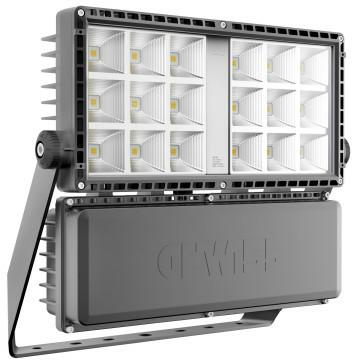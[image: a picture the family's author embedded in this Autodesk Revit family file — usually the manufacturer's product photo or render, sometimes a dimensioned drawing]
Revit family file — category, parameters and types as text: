
# Revit family: Lighting-Floodlights-GEWISS-SMART[PRO]2.0-LED-MEDIUM-POWER_2MODULE_DALI.CLI
name_source: partatom
category: Apparecchi per illuminazione
units: mm (PartAtom-declared; Revit-internal decimal feet)

## family parameters
Condiviso = No
Host = Superficie
Punto di calcolo locali = No
Quota connettore circolare = Usa diametro
Sorgente d'illuminazione = No
Taglio con vuoti quando caricato = No
Tipo di parte = Normale

## types (1)
- Lighting-Floodlights-GEWISS-SMART[PRO]2.0-LED-MEDIUM-POWER_2MODULE_DALI.CLI
    Applicazione = Indoor / Outdoor
    Body = Die-cast aluminium -
    Catalogue = LIGHTING
    Classification: = -
    Color Rendering Index = CRI-80
    Colour = Graphite grey
    Colour : = Polyester powder coated
    Colour temperature = 5700K
    Context = Sport, Big Areas
    Control System = DALI
    DIN 18032-3 certification = Yes
    Descrizione = SMARTPRO2.0 2M 5700K CRI80 A3 DALI CL1
    Device with reduced surface temperature = No
    Driver = Included
    Driver Box = Built-in
    Efficiency (lm/W) = 113
    Eletrical and lighting features = -
    External screw = Stainless steel
    Fixing = Bracket
    GW - Codice Electrocod = 2424
    Gasket = Anti-aging silicone
    General information = -
    Glow Wire Test : = -
    IDF = fea9197c-9a36-4712-b795-7101e1c42ea6
    IDT = 256691c01990452284852cf61e57a00c
    IP degree = IP66
    IPEA = ROAD = A // LARGE AREAS = A3 + // CYCLOPEDONALS = A + // GREEN AREAS = A + // HISTORICAL CENTER = A5 + // OTHER = A5 +
    Immagine tipo = GWP2274AD.jpg
    Installationa and maintenance = -
    Insulation class = I
    LED Maintenance = Not available
    Lampada = LED
    Lifetime = L90B10 (Tq+25°C) - 40000h L90B10 (Tq+50°C) = 32000h L80B10 (Tq+25°C) - 90000h
    Locking Hook = Hexagonal metric screws
    Lumen output (lm) = 37200
    Luminaire = LED luminaire with small,mid and high lumen power
    Materials = -
    Maximum surface exposed to the wind : = 0,170 m2
    Modello = GWP2285ND
    Mouting and installation = High-mast lighting - Wall mounting - Ground mouting
    Operating temperature : = -30 +50 °C
    Optic = A3 - Assymetric Narrow
    Optic : = Polished anodised aluminum reflector with 99.99% pure aluminum
    Optic Maintenance = Not available
    Optic and illuminating features = -
    Overvoltage protection = DM 6 kV / CM 10 kV
    Photobiological Risk Class = -
    Produttore = GEWISS S.p.A.
    Prospetto di default = 1219 mm
    Rated frequency (Hz) = 50 / 60
    SEO = Floodlight
    Shield type = Flat tempered glass 4mm
    Shock resistance = IK08
    Spostamento_x = 2186 mm
    Spostamento_x_effettivo = 1814 mm
    Standard Deviation Colour Matching = SDCM = 3
    Standard- = EN60598-1; EN60598-2-5; IEC 62778; IEC 62471; EN13201
    Standards and approvals = -
    Stocking temperature = -
    Supply voltage = 220 - 240 V
    System power = 330W
    Technical sheet = https://www.gewiss.com
    Tilt- = Rotation on bracket with integrated goniometer
    Type of light source = LED - Not replaceable
    URL = https://www.gewiss.com
    Unified Glare Rating = G*6 - ULOR = 0
    Unique digital code (Datamatrix) = Currently not present
    Version file RFA = 20.11
    Versions = 5700K cold light
    Warranty = 5 years
    Weight (kg): = 13
    Wiring = Watertight connector
